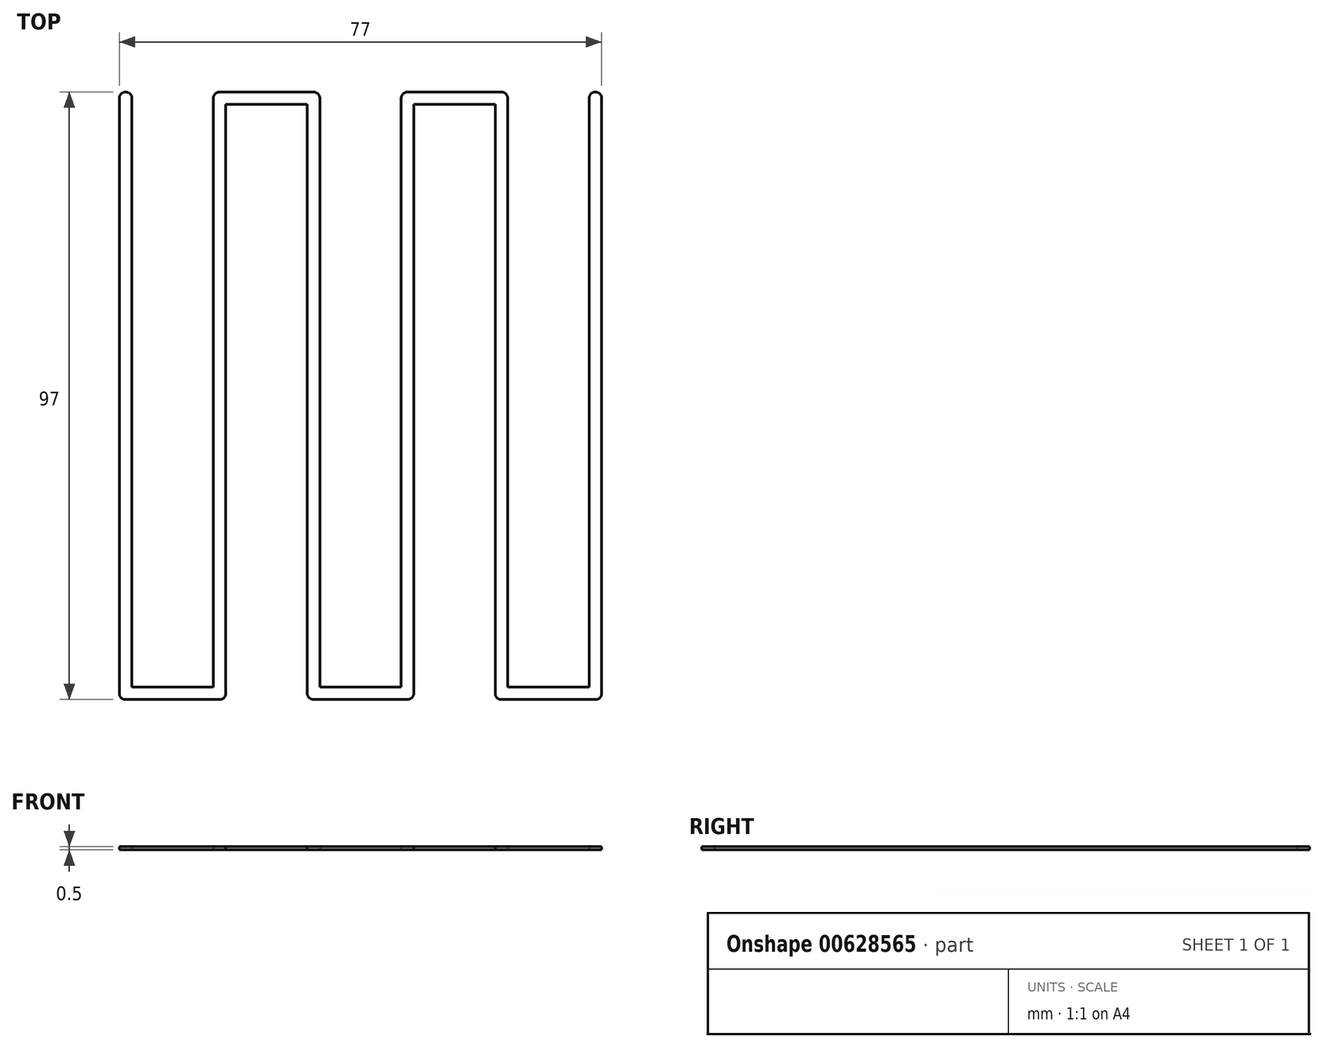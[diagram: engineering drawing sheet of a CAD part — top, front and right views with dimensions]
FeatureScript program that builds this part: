
annotation { "Feature Type Name" : "Feature", "Feature Type Description" : "" }
export const myFeature = defineFeature(function(context is Context, id is Id, definition is map)
    precondition{}
    {
        {
            var Q0;
            Q0=qCreatedBy(makeId("Top.planeOp"),FACE);
            var sketch = newSketch(context, id + "F0", { "sketchPlane" : qUnion([Q0])});
            skLineSegment(sketch, "E0.bottom", {"start": v(-50, 50) * mm, "end": v(50, 50) * mm, "construction": true});
            skLineSegment(sketch, "E0.top", {"start": v(-50, -50) * mm, "end": v(50, -50) * mm, "construction": true});
            skLineSegment(sketch, "E0.left", {"start": v(-50, 50) * mm, "end": v(-50, -50) * mm, "construction": true});
            skLineSegment(sketch, "E0.right", {"start": v(50, 50) * mm, "end": v(50, -50) * mm, "construction": true});
            skPoint(sketch, "E1", {"position": v(50, 0) * mm});
            skPoint(sketch, "E2", {"position": v(0, 50) * mm});
            skSolve(sketch);
        }
        {
            var Q0;
            Q0=qCreatedBy(makeId("Top.planeOp"),FACE);
            var sketch = newSketch(context, id + "F1", { "sketchPlane" : qUnion([Q0])});
            skLineSegment(sketch, "E3", {"start": v(37, 47.5) * mm, "end": v(37, -47.5) * mm});
            skLineSegment(sketch, "E4", {"start": v(37, -47.5) * mm, "end": v(22, -47.5) * mm});
            skLineSegment(sketch, "E5", {"start": v(22, -47.5) * mm, "end": v(22, 47.5) * mm});
            skLineSegment(sketch, "E6", {"start": v(22, 47.5) * mm, "end": v(7, 47.5) * mm});
            skLineSegment(sketch, "E7", {"start": v(7, 47.5) * mm, "end": v(7, -47.5) * mm});
            skLineSegment(sketch, "E8", {"start": v(7, -47.5) * mm, "end": v(-8, -47.5) * mm});
            skLineSegment(sketch, "E9", {"start": v(-8, -47.5) * mm, "end": v(-8, 47.5) * mm});
            skLineSegment(sketch, "E10", {"start": v(-8, 47.5) * mm, "end": v(-23, 47.5) * mm});
            skLineSegment(sketch, "E11", {"start": v(-23, 47.5) * mm, "end": v(-23, -47.5) * mm});
            skLineSegment(sketch, "E12", {"start": v(-23, -47.5) * mm, "end": v(-38, -47.5) * mm});
            skLineSegment(sketch, "E13", {"start": v(-38, -47.5) * mm, "end": v(-38, 47.5) * mm});
            skPoint(sketch, "E14", {"position": v(37, 0) * mm});
            skArc(sketch, "E15.0.startCap", {"start": v(-37, -47.5) * mm, "mid": v(-38, -48.5) * mm, "end": v(-39, -47.5) * mm});
            skArc(sketch, "E15.0.endCap", {"start": v(-39, 47.5) * mm, "mid": v(-38, 48.5) * mm, "end": v(-37, 47.5) * mm});
            skLineSegment(sketch, "E15.0.left", {"start": v(-39, -47.5) * mm, "end": v(-39, 47.5) * mm});
            skLineSegment(sketch, "E15.0.right", {"start": v(-37, -47.5) * mm, "end": v(-37, 47.5) * mm});
            skArc(sketch, "E15.1.startCap", {"start": v(36, 47.5) * mm, "mid": v(37, 48.5) * mm, "end": v(38, 47.5) * mm});
            skArc(sketch, "E15.1.endCap", {"start": v(38, -47.5) * mm, "mid": v(37, -48.5) * mm, "end": v(36, -47.5) * mm});
            skLineSegment(sketch, "E15.1.left", {"start": v(38, 47.5) * mm, "end": v(38, -47.5) * mm});
            skLineSegment(sketch, "E15.1.right", {"start": v(36, 47.5) * mm, "end": v(36, -47.5) * mm});
            skArc(sketch, "E15.2.startCap", {"start": v(23, -47.5) * mm, "mid": v(22, -48.5) * mm, "end": v(21, -47.5) * mm});
            skArc(sketch, "E15.2.endCap", {"start": v(21, 47.5) * mm, "mid": v(22, 48.5) * mm, "end": v(23, 47.5) * mm});
            skLineSegment(sketch, "E15.2.left", {"start": v(21, -47.5) * mm, "end": v(21, 47.5) * mm});
            skLineSegment(sketch, "E15.2.right", {"start": v(23, -47.5) * mm, "end": v(23, 47.5) * mm});
            skArc(sketch, "E15.3.startCap", {"start": v(-23, -46.5) * mm, "mid": v(-22, -47.5) * mm, "end": v(-23, -48.5) * mm});
            skArc(sketch, "E15.3.endCap", {"start": v(-38, -48.5) * mm, "mid": v(-39, -47.5) * mm, "end": v(-38, -46.5) * mm});
            skLineSegment(sketch, "E15.3.left", {"start": v(-23, -48.5) * mm, "end": v(-38, -48.5) * mm});
            skLineSegment(sketch, "E15.3.right", {"start": v(-23, -46.5) * mm, "end": v(-38, -46.5) * mm});
            skArc(sketch, "E15.4.startCap", {"start": v(37, -46.5) * mm, "mid": v(38, -47.5) * mm, "end": v(37, -48.5) * mm});
            skArc(sketch, "E15.4.endCap", {"start": v(22, -48.5) * mm, "mid": v(21, -47.5) * mm, "end": v(22, -46.5) * mm});
            skLineSegment(sketch, "E15.4.left", {"start": v(37, -48.5) * mm, "end": v(22, -48.5) * mm});
            skLineSegment(sketch, "E15.4.right", {"start": v(37, -46.5) * mm, "end": v(22, -46.5) * mm});
            skArc(sketch, "E15.5.startCap", {"start": v(22, 48.5) * mm, "mid": v(23, 47.5) * mm, "end": v(22, 46.5) * mm});
            skArc(sketch, "E15.5.endCap", {"start": v(7, 46.5) * mm, "mid": v(6, 47.5) * mm, "end": v(7, 48.5) * mm});
            skLineSegment(sketch, "E15.5.left", {"start": v(22, 46.5) * mm, "end": v(7, 46.5) * mm});
            skLineSegment(sketch, "E15.5.right", {"start": v(22, 48.5) * mm, "end": v(7, 48.5) * mm});
            skArc(sketch, "E15.6.startCap", {"start": v(6, 47.5) * mm, "mid": v(7, 48.5) * mm, "end": v(8, 47.5) * mm});
            skArc(sketch, "E15.6.endCap", {"start": v(8, -47.5) * mm, "mid": v(7, -48.5) * mm, "end": v(6, -47.5) * mm});
            skLineSegment(sketch, "E15.6.left", {"start": v(8, 47.5) * mm, "end": v(8, -47.5) * mm});
            skLineSegment(sketch, "E15.6.right", {"start": v(6, 47.5) * mm, "end": v(6, -47.5) * mm});
            skArc(sketch, "E15.7.startCap", {"start": v(-24, 47.5) * mm, "mid": v(-23, 48.5) * mm, "end": v(-22, 47.5) * mm});
            skArc(sketch, "E15.7.endCap", {"start": v(-22, -47.5) * mm, "mid": v(-23, -48.5) * mm, "end": v(-24, -47.5) * mm});
            skLineSegment(sketch, "E15.7.left", {"start": v(-22, 47.5) * mm, "end": v(-22, -47.5) * mm});
            skLineSegment(sketch, "E15.7.right", {"start": v(-24, 47.5) * mm, "end": v(-24, -47.5) * mm});
            skArc(sketch, "E15.8.startCap", {"start": v(-8, 48.5) * mm, "mid": v(-7, 47.5) * mm, "end": v(-8, 46.5) * mm});
            skArc(sketch, "E15.8.endCap", {"start": v(-23, 46.5) * mm, "mid": v(-24, 47.5) * mm, "end": v(-23, 48.5) * mm});
            skLineSegment(sketch, "E15.8.left", {"start": v(-8, 46.5) * mm, "end": v(-23, 46.5) * mm});
            skLineSegment(sketch, "E15.8.right", {"start": v(-8, 48.5) * mm, "end": v(-23, 48.5) * mm});
            skArc(sketch, "E15.9.startCap", {"start": v(7, -46.5) * mm, "mid": v(8, -47.5) * mm, "end": v(7, -48.5) * mm});
            skArc(sketch, "E15.9.endCap", {"start": v(-8, -48.5) * mm, "mid": v(-9, -47.5) * mm, "end": v(-8, -46.5) * mm});
            skLineSegment(sketch, "E15.9.left", {"start": v(7, -48.5) * mm, "end": v(-8, -48.5) * mm});
            skLineSegment(sketch, "E15.9.right", {"start": v(7, -46.5) * mm, "end": v(-8, -46.5) * mm});
            skArc(sketch, "E15.10.startCap", {"start": v(-7, -47.5) * mm, "mid": v(-8, -48.5) * mm, "end": v(-9, -47.5) * mm});
            skArc(sketch, "E15.10.endCap", {"start": v(-9, 47.5) * mm, "mid": v(-8, 48.5) * mm, "end": v(-7, 47.5) * mm});
            skLineSegment(sketch, "E15.10.left", {"start": v(-9, -47.5) * mm, "end": v(-9, 47.5) * mm});
            skLineSegment(sketch, "E15.10.right", {"start": v(-7, -47.5) * mm, "end": v(-7, 47.5) * mm});
            skSolve(sketch);
        }
        {
            var Q0;
            Q0 = qSketchRegion(id + "F1", true);
            extrude(context, id + "F2", {"entities" : qUnion([Q0]), "depth" : .5 * mm, "offsetDistance" : 25 * mm});
        }
    });
